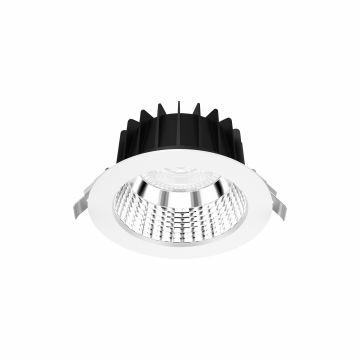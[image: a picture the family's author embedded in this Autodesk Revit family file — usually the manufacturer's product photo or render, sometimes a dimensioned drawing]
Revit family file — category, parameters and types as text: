
# Revit family: Lighting-CommercialSector-GEWISS-ELIA-AL-LED_ACCENT_D145
name_source: partatom
category: Apparecchi per illuminazione
units: mm (PartAtom-declared; Revit-internal decimal feet)

## family parameters
Condiviso = No
Host = Superficie
Punto di calcolo locali = Sì
Quota connettore circolare = Usa diametro
Sorgente d'illuminazione = Sì
Taglio con vuoti quando caricato = No
Tipo di parte = Normale

## types (16) — shared parameters
Angolo inclinazione = -90.00°
Application = Indoor
Catalogue = LIGHTING
Catalogue Range = ELIA AL
Colour = White
Dimensions (mm) = Standard
Emetti da lunghezza linea = 610 mm
FORO_CONTROSOFFITTO = 80 mm  [stored 0.262467 ft]
File diagramma fotometrico = GWF1411GH940.IES
Filtro dei colori = 16777215
IDF = d571a108-c869-40b6-9e34-3f4df16e1d93
IDT = 40448338-f630-44a4-b37d-0c013efb62a7
IP degree = IP40 - IP54
Immagine tipo = ELIA_AL.jpg
Installation = Flush mounted
Insulation class = II
LARGHEZZA_FORO = 820 mm
LED = <Per categoria>
LED Life time (L80B50) = L80 B50 (Tq25°) = 50.000h
LUNGHEZZA FORO = 969 mm
L_lampada = 1500 mm
Lamp = LED
Operating temperature: = -20° +45°
POSIZIONE = 80000
Produttore = GEWISS S.p.A.
Prospetto di default = 1219 mm
SEO = Flush mounted
STRUTTURA = <Per categoria>
Shock resistance = IK06
System power = 18W
Technical sheet = https://www.gewiss.com
Type of lamp = LED
Type of light source = LED - Not replaceable
Typology = Flush mounted
UGR: = UGR<19
URL = https://www.gewiss.com
Variazione temperatura colore lampada con luminosità attenuata = <Nessuno>
Version file RFA = 20.0
Voltage = 220-240 VÂ
Warranty = 5 years
Weight (kg) = 0,5
Weight (kg): = 0,5
Working temperature = -20° +45°

## per-type parameters (varying)
| type | Colour temperature | Colour temperature: | Descrizione | Lumen output (lm) | Modello | Optic |
| GWF1410GG930 - ELIA AL S2 30K 36° ST.ALONE ON/OFF CRI90 | 3000K | 3000K | ELIA AL S2 30K 36° ST.ALONE ON/OFF CRI90 | 1700 | GWF1410GG930 | 36° |
| GWF1411GH840 - ELIA AL S2 40K 60° ST.ALONE DALI CRI80 | 4000K | 4000K | ELIA AL S2 40K 60° ST.ALONE DALI CRI80 | 2120 | GWF1411GH840 | 60° |
| GWF1410GH930 - ELIA AL S2 30K 60° ST.ALONE ON/OFF CRI90 | 3000K | 3000K | ELIA AL S2 30K 60° ST.ALONE ON/OFF CRI90 | 1790 | GWF1410GH930 | 60° |
| GWF1410GH840 - ELIA AL S2 40K 60° ST.ALONE ON/OFF CRI80 | 4000K | 4000K | ELIA AL S2 40K 60° ST.ALONE ON/OFF CRI80 | 2120 | GWF1410GH840 | 60° |
| GWF1411GG840 - ELIA AL S2 40K 36° ST.ALONE DALI CRI80 | 4000K | 4000K | ELIA AL S2 40K 36° ST.ALONE DALI CRI80 | 2030 | GWF1411GG840 | 36° |
| GWF1411GH930 - ELIA AL S2 30K 60° ST.ALONE DALI CRI90 | 3000K | 3000K | ELIA AL S2 30K 60° ST.ALONE DALI CRI90 | 1790 | GWF1411GH930 | 60° |
| GWF1410GG830 - ELIA AL S2 30K 36° ST.ALONE ON/OFF CRI80 | 3000K | 3000K | ELIA AL S2 30K 36° ST.ALONE ON/OFF CRI80 | 1900 | GWF1410GG830 | 36° |
| GWF1411GH830 - ELIA AL S2 30K 60° ST.ALONE DALI CRI80 | 3000K | 3000K | ELIA AL S2 30K 60° ST.ALONE DALI CRI80 | 1990 | GWF1411GH830 | 60° |
| GWF1410GH940 - ELIA AL S2 40K 60° ST.ALONE ON/OFF CRI90 | 4000K | 4000K | ELIA AL S2 40K 60° ST.ALONE ON/OFF CRI90 | 1900 | GWF1410GH940 | 60° |
| GWF1410GG940 - ELIA AL S2 40K 36° ST.ALONE ON/OFF CRI90 | 4000K | 4000K | ELIA AL S2 40K 36° ST.ALONE ON/OFF CRI90 | 1800 | GWF1410GG940 | 36° |
| GWF1411GG940 - ELIA AL S2 40K 36° ST.ALONE DALI CRI90 | 4000K | 4000K | ELIA AL S2 40K 36° ST.ALONE DALI CRI90 | 1800 | GWF1411GG940 | 36° |
| GWF1411GG830 - ELIA AL S2 30K 36° ST.ALONE DALI CRI80 | 3000K | 3000K | ELIA AL S2 30K 36° ST.ALONE DALI CRI80 | 1900 | GWF1411GG830 | 36° |
| GWF1410GH830 - ELIA AL S2 30K 60° ST.ALONE ON/OFF CRI80 | 3000K | 3000K | ELIA AL S2 30K 60° ST.ALONE ON/OFF CRI80 | 1990 | GWF1410GH830 | 60° |
| GWF1411GH940 - ELIA AL S2 40K 60° ST.ALONE DALI CRI90 | 4000K | 4000K | ELIA AL S2 40K 60° ST.ALONE DALI CRI90 | 1900 | GWF1411GH940 | 60° |
| GWF1411GG930 - ELIA AL S2 30K 36° ST.ALONE DALI CRI90 | 3000K | 3000K | ELIA AL S2 30K 36° ST.ALONE DALI CRI90 | 1700 | GWF1411GG930 | 36° |
| GWF1410GG840 - ELIA AL S2 40K 36° ST.ALONE ON/OFF CRI80 | 4000K | 4000K | ELIA AL S2 40K 36° ST.ALONE ON/OFF CRI80 | 2030 | GWF1410GG840 | 36° |

note: [stored X ft] marks values corroborated as IEEE doubles in the binary element streams (Revit-internal decimal feet)
